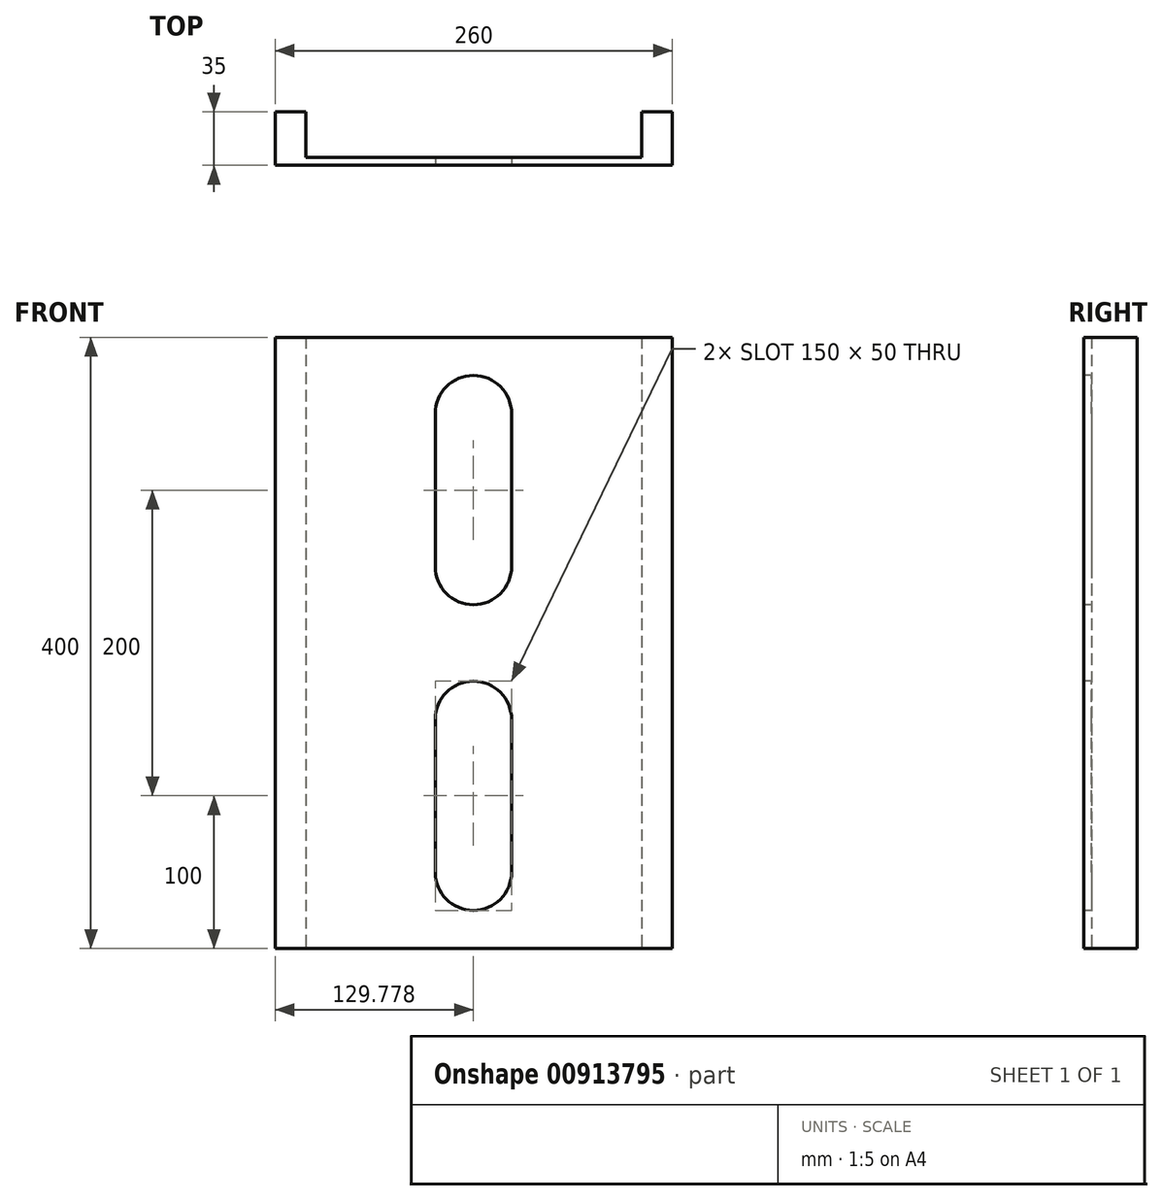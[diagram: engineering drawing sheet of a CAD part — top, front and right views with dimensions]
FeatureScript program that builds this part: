
annotation { "Feature Type Name" : "Feature", "Feature Type Description" : "" }
export const myFeature = defineFeature(function(context is Context, id is Id, definition is map)
    precondition{}
    {
        {
            var Q0;
            Q0=qCreatedBy(makeId("Top.planeOp"),FACE);
            var sketch = newSketch(context, id + "F0", { "sketchPlane" : qUnion([Q0])});
            skLineSegment(sketch, "E0.bottom", {"start": v(-130, -17.5) * mm, "end": v(130, -17.5) * mm});
            skLineSegment(sketch, "E0.top", {"start": v(-130, 17.5) * mm, "end": v(-110, 17.5) * mm});
            skLineSegment(sketch, "E0.left", {"start": v(-130, -17.5) * mm, "end": v(-130, 17.5) * mm});
            skLineSegment(sketch, "E0.right", {"start": v(130, -17.5) * mm, "end": v(130, 17.5) * mm});
            skPoint(sketch, "E0.middle", {"position": v(0, 0) * mm});
            skLineSegment(sketch, "E1.top", {"start": v(-110, -12.5) * mm, "end": v(110, -12.5) * mm});
            skLineSegment(sketch, "E1.left", {"start": v(-110, 17.5) * mm, "end": v(-110, -12.5) * mm});
            skLineSegment(sketch, "E1.right", {"start": v(110, 17.5) * mm, "end": v(110, -12.5) * mm});
            skLineSegment(sketch, "E2.trimOffspring", {"start": v(110, 17.5) * mm, "end": v(130, 17.5) * mm});
            skSolve(sketch);
        }
        {
            var Q0;
            Q0=makeQuery(id+"F0.imprint","IMPRINT",FACE,{"disambiguationData":[TD([[makeQuery(id+"F0.imprint","IMPRINT",EDGE,{"derivedFrom":sQuery(id+"F0.wireOp",EDGE,"E0.bottom")}),1.0]])]});
            extrude(context, id + "F1", {"entities" : qUnion([Q0]), "depth" : 400 * mm, "offsetDistance" : 25 * mm});
        }
        {
            var Q0;
            Q0=makeQuery(id+"F1.opExtrude","SWEPT_FACE",FACE,{"disambiguationData":[OSD([sQuery(id+"F0.wireOp",EDGE,"E0.bottom")])]});
            var sketch = newSketch(context, id + "F2", { "sketchPlane" : qUnion([Q0])});
            skLineSegment(sketch, "E3.left", {"start": v(-25.22, 250) * mm, "end": v(-25.22, 350) * mm});
            skLineSegment(sketch, "E3.right", {"start": v(24.78, 250) * mm, "end": v(24.78, 350) * mm});
            skPoint(sketch, "E3.middle", {"position": v(-0.22, 300) * mm});
            skArc(sketch, "E4", {"start": v(-25.22, 350) * mm, "mid": v(-0.22, 375) * mm, "end": v(24.78, 350) * mm});
            skArc(sketch, "E5", {"start": v(24.78, 250) * mm, "mid": v(-0.22, 225) * mm, "end": v(-25.22, 250) * mm});
            skLineSegment(sketch, "E6", {"start": v(-151.6, 200) * mm, "end": v(155.6, 200) * mm, "construction": true});
            skLineSegment(sketch, "E7.MirrorCS", {"start": v(24.78, 150) * mm, "end": v(24.78, 50) * mm});
            skLineSegment(sketch, "E8.MirrorCS", {"start": v(-25.22, 150) * mm, "end": v(-25.22, 50) * mm});
            skArc(sketch, "E9.MirrorCS", {"start": v(-25.22, 50) * mm, "mid": v(-0.22, 25) * mm, "end": v(24.78, 50) * mm});
            skArc(sketch, "E10.MirrorCS", {"start": v(24.78, 150) * mm, "mid": v(-0.22, 175) * mm, "end": v(-25.22, 150) * mm});
            skSolve(sketch);
        }
        {
            var Q0;
            Q0 = qSketchRegion(id + "F2", true);
            extrude(context, id + "F3", {"entities" : qUnion([Q0]), "operationType" : NewBodyOperationType.REMOVE, "oppositeDirection" : true, "depth" : 25 * mm, "offsetDistance" : 25 * mm});
        }
    });
